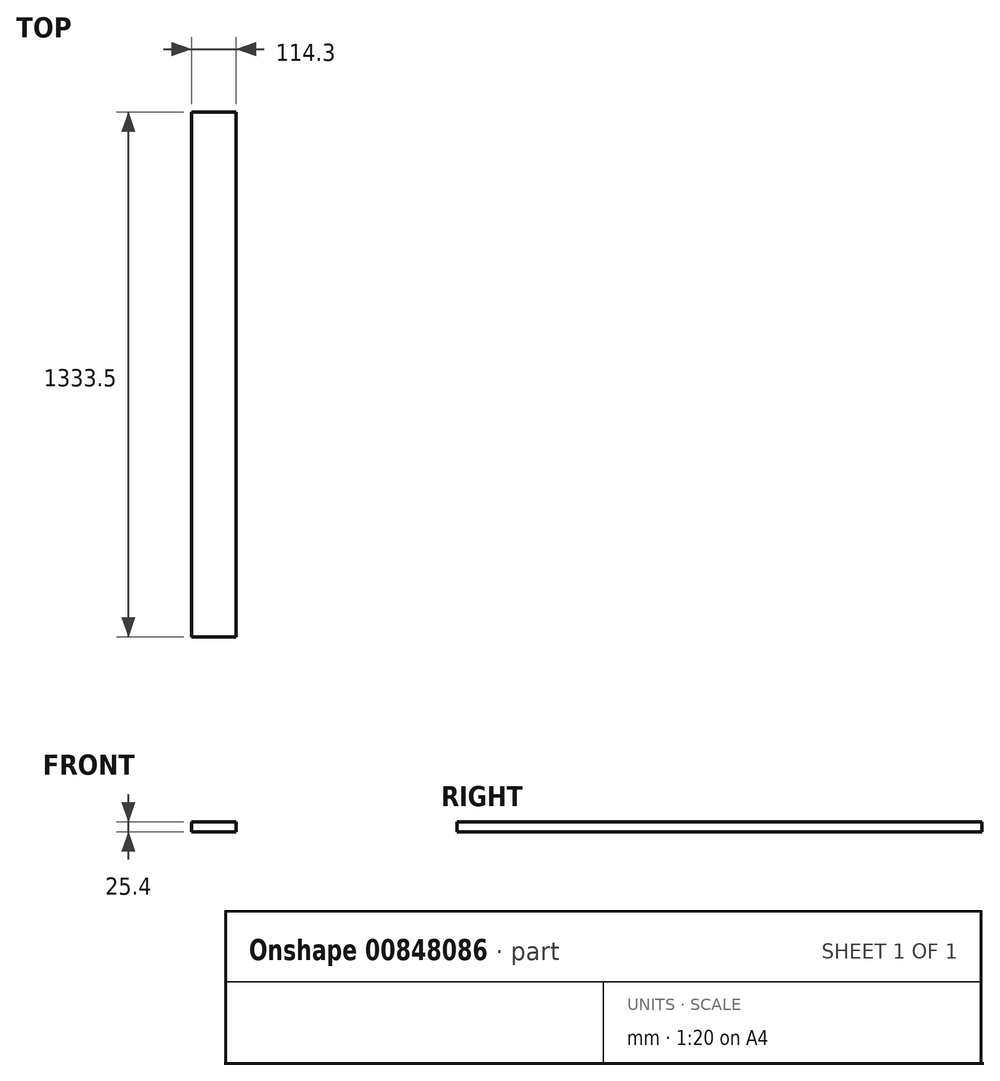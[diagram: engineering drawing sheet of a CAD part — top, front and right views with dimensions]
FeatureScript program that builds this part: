
annotation { "Feature Type Name" : "Feature", "Feature Type Description" : "" }
export const myFeature = defineFeature(function(context is Context, id is Id, definition is map)
    precondition{}
    {
        {
            var Q0;
            Q0=qCreatedBy(makeId("Top.planeOp"),FACE);
            var sketch = newSketch(context, id + "F0", { "sketchPlane" : qUnion([Q0])});
            skLineSegment(sketch, "E0.bottom", {"start": v(57.15, 666.75) * mm, "end": v(-57.15, 666.75) * mm});
            skLineSegment(sketch, "E0.top", {"start": v(57.15, -666.75) * mm, "end": v(-57.15, -666.75) * mm});
            skLineSegment(sketch, "E0.left", {"start": v(57.15, 666.75) * mm, "end": v(57.15, -666.75) * mm});
            skLineSegment(sketch, "E0.right", {"start": v(-57.15, 666.75) * mm, "end": v(-57.15, -666.75) * mm});
            skPoint(sketch, "E0.middle", {"position": v(0, 0) * mm});
            skSolve(sketch);
        }
        {
            var Q0;
            Q0=makeQuery(id+"F0.imprint","IMPRINT",FACE,{"disambiguationData":[TD([[makeQuery(id+"F0.imprint","IMPRINT",EDGE,{"derivedFrom":sQuery(id+"F0.wireOp",EDGE,"E0.bottom")}),1.0]])]});
            extrude(context, id + "F1", {"entities" : qUnion([Q0]), "depth" : 25.4 * mm, "offsetDistance" : 25.4 * mm});
        }
    });
